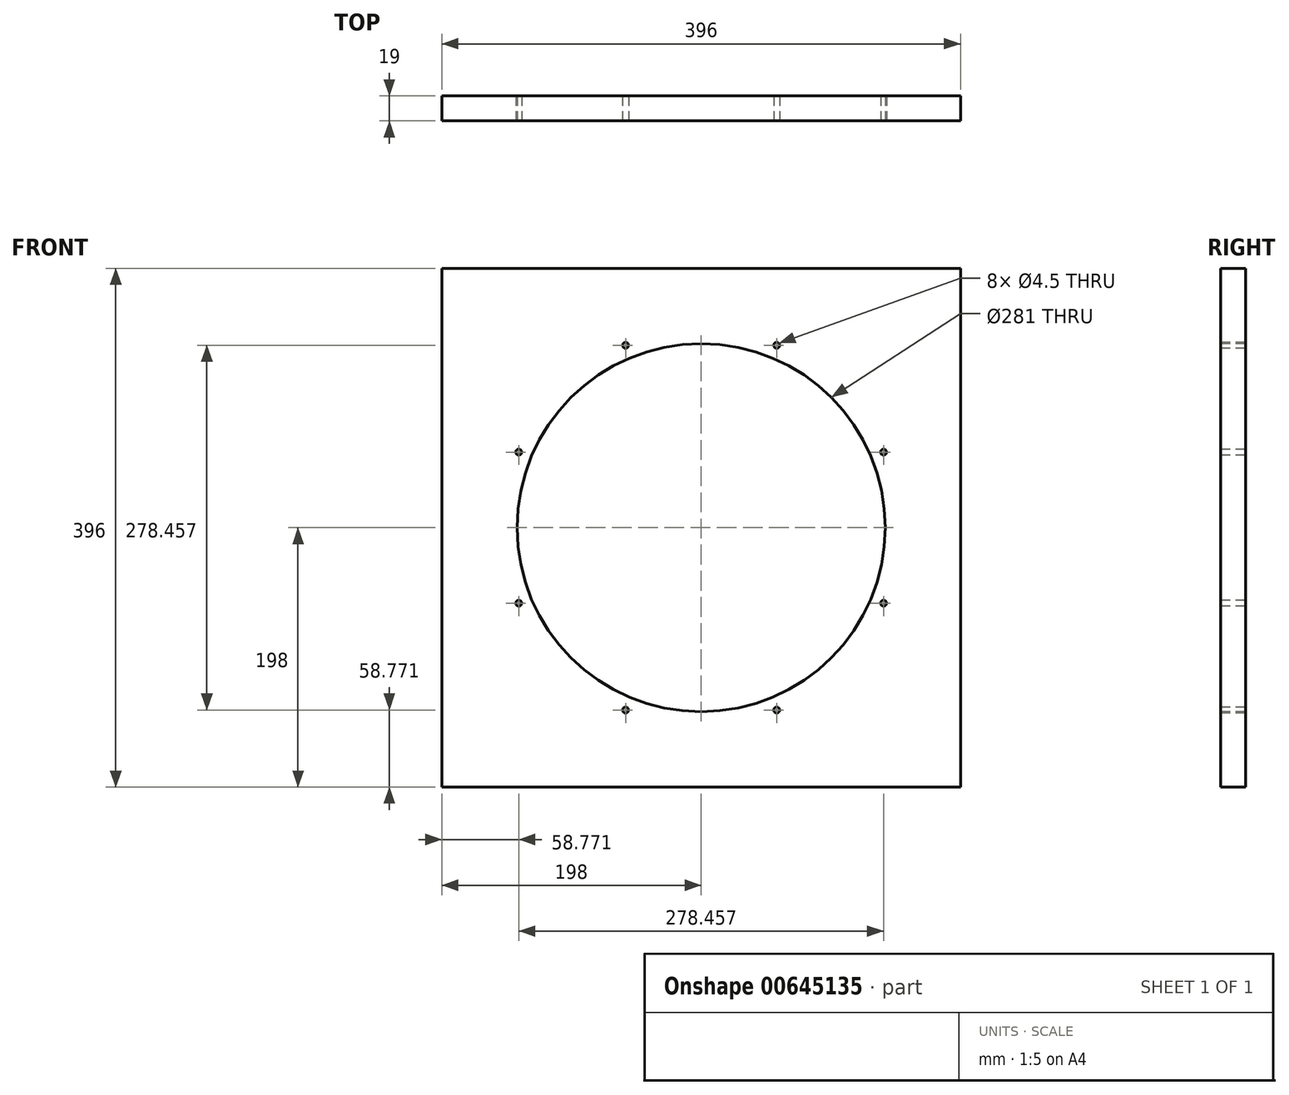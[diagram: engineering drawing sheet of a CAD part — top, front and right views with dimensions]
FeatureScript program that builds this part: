
annotation { "Feature Type Name" : "Feature", "Feature Type Description" : "" }
export const myFeature = defineFeature(function(context is Context, id is Id, definition is map)
    precondition{}
    {
        {
            var Q0;
            Q0=qCreatedBy(makeId("Front.planeOp"),FACE);
            var sketch = newSketch(context, id + "F0", { "sketchPlane" : qUnion([Q0])});
            skLineSegment(sketch, "E0.bottom", {"start": v(198, -198) * mm, "end": v(-198, -198) * mm});
            skLineSegment(sketch, "E0.top", {"start": v(198, 198) * mm, "end": v(-198, 198) * mm});
            skLineSegment(sketch, "E0.left", {"start": v(198, -198) * mm, "end": v(198, 198) * mm});
            skLineSegment(sketch, "E0.right", {"start": v(-198, -198) * mm, "end": v(-198, 198) * mm});
            skPoint(sketch, "E0.middle", {"position": v(0, 0) * mm});
            skSolve(sketch);
        }
        {
            var Q0;
            Q0 = qSketchRegion(id + "F0", true);
            extrude(context, id + "F1", {"entities" : qUnion([Q0]), "depth" : 19 * mm, "offsetDistance" : 25.4 * mm});
        }
        {
            var Q0;
            Q0=makeQuery(id+"F1.opExtrude","CAP_FACE",FACE,{"disambiguationData":[OSD([sQuery(id+"F0.wireOp",EDGE,"E0.bottom"),sQuery(id+"F0.wireOp",EDGE,"E0.top"),sQuery(id+"F0.wireOp",EDGE,"E0.left"),sQuery(id+"F0.wireOp",EDGE,"E0.right")])],"isStart":false});
            var sketch = newSketch(context, id + "F2", { "sketchPlane" : qUnion([Q0])});
            skCircle(sketch, "E1", {"center": v(0, 0) * mm, "radius": 140.5 * mm});
            skSolve(sketch);
        }
        {
            var Q0;
            Q0 = qSketchRegion(id + "F2", true);
            extrude(context, id + "F3", {"entities" : qUnion([Q0]), "operationType" : NewBodyOperationType.REMOVE, "oppositeDirection" : true, "depth" : 25.4 * mm, "offsetDistance" : 25.4 * mm});
        }
        {
            var Q0;
            Q0=makeQuery(id+"F1.opExtrude","CAP_FACE",FACE,{"disambiguationData":[OSD([sQuery(id+"F0.wireOp",EDGE,"E0.bottom"),sQuery(id+"F0.wireOp",EDGE,"E0.top"),sQuery(id+"F0.wireOp",EDGE,"E0.left"),sQuery(id+"F0.wireOp",EDGE,"E0.right")])],"isStart":false});
            var sketch = newSketch(context, id + "F4", { "sketchPlane" : qUnion([Q0])});
            skCircle(sketch, "E2", {"center": v(0, 0) * mm, "radius": 150.7 * mm, "construction": true});
            skLineSegment(sketch, "E3", {"start": v(0, 0) * mm, "end": v(0, 150.7) * mm, "construction": true});
            skLineSegment(sketch, "E4", {"start": v(0, 0) * mm, "end": v(57.67, 139.23) * mm, "construction": true});
            skLineSegment(sketch, "E5", {"start": v(0, 0) * mm, "end": v(139.23, 57.67) * mm, "construction": true});
            skLineSegment(sketch, "E6", {"start": v(0, 0) * mm, "end": v(139.23, -57.67) * mm, "construction": true});
            skLineSegment(sketch, "E7", {"start": v(0, 0) * mm, "end": v(57.67, -139.23) * mm, "construction": true});
            skLineSegment(sketch, "E8", {"start": v(0, 0) * mm, "end": v(-57.67, -139.23) * mm, "construction": true});
            skLineSegment(sketch, "E9", {"start": v(0, 0) * mm, "end": v(-139.23, -57.67) * mm, "construction": true});
            skLineSegment(sketch, "E10", {"start": v(0, 0) * mm, "end": v(-139.23, 57.67) * mm, "construction": true});
            skLineSegment(sketch, "E11", {"start": v(0, 0) * mm, "end": v(-57.67, 139.23) * mm, "construction": true});
            skCircle(sketch, "E12", {"center": v(57.67, 139.23) * mm, "radius": 2.25 * mm});
            skCircle(sketch, "E13", {"center": v(139.23, 57.67) * mm, "radius": 2.25 * mm});
            skCircle(sketch, "E14", {"center": v(139.23, -57.67) * mm, "radius": 2.25 * mm});
            skCircle(sketch, "E15", {"center": v(57.67, -139.23) * mm, "radius": 2.25 * mm});
            skCircle(sketch, "E16", {"center": v(-57.67, -139.23) * mm, "radius": 2.25 * mm});
            skCircle(sketch, "E17", {"center": v(-139.23, -57.67) * mm, "radius": 2.25 * mm});
            skCircle(sketch, "E18", {"center": v(-139.23, 57.67) * mm, "radius": 2.25 * mm});
            skCircle(sketch, "E19", {"center": v(-57.67, 139.23) * mm, "radius": 2.25 * mm});
            skSolve(sketch);
        }
        {
            var Q0;
            Q0 = qSketchRegion(id + "F4", true);
            extrude(context, id + "F5", {"entities" : qUnion([Q0]), "operationType" : NewBodyOperationType.REMOVE, "oppositeDirection" : true, "depth" : 25.4 * mm, "offsetDistance" : 25.4 * mm});
        }
    });
